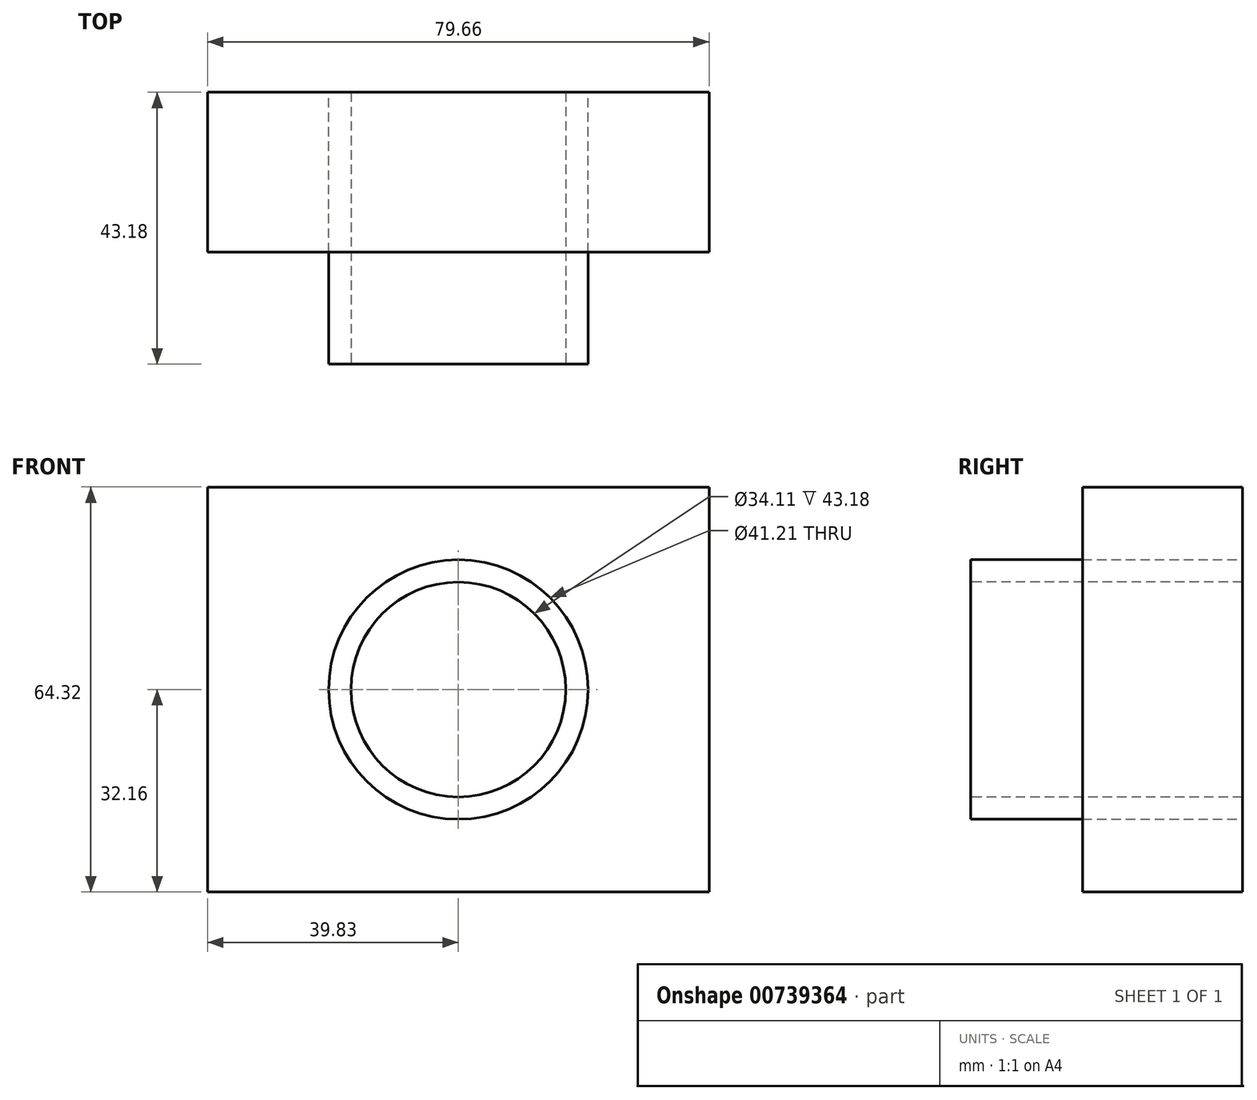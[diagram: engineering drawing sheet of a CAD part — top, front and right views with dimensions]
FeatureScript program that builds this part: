
annotation { "Feature Type Name" : "Feature", "Feature Type Description" : "" }
export const myFeature = defineFeature(function(context is Context, id is Id, definition is map)
    precondition{}
    {
        {
            var Q0;
            Q0=qCreatedBy(makeId("Front.planeOp"),FACE);
            var sketch = newSketch(context, id + "F0", { "sketchPlane" : qUnion([Q0])});
            skLineSegment(sketch, "E0.bottom", {"start": v(39.83, 32.16) * mm, "end": v(-39.83, 32.16) * mm});
            skLineSegment(sketch, "E0.top", {"start": v(39.83, -32.16) * mm, "end": v(-39.83, -32.16) * mm});
            skLineSegment(sketch, "E0.left", {"start": v(39.83, 32.16) * mm, "end": v(39.83, -32.16) * mm});
            skLineSegment(sketch, "E0.right", {"start": v(-39.83, 32.16) * mm, "end": v(-39.83, -32.16) * mm});
            skPoint(sketch, "E0.middle", {"position": v(0, 0) * mm});
            skCircle(sketch, "E1", {"center": v(0, 0) * mm, "radius": 20.6 * mm});
            skSolve(sketch);
        }
        {
            var Q0;
            Q0=makeQuery(id+"F0.imprint","IMPRINT",FACE,{"disambiguationData":[TD([[makeQuery(id+"F0.imprint","IMPRINT",EDGE,{"derivedFrom":sQuery(id+"F0.wireOp",EDGE,"E0.bottom")}),1.0]])]});
            extrude(context, id + "F1", {"entities" : qUnion([Q0]), "depth" : 25.4 * mm, "offsetDistance" : 25.4 * mm});
        }
        {
            var Q0;
            Q0=makeQuery(id+"F1.opExtrude","CAP_FACE",FACE,{"disambiguationData":[OSD([sQuery(id+"F0.wireOp",EDGE,"E0.bottom"),sQuery(id+"F0.wireOp",EDGE,"E0.top"),sQuery(id+"F0.wireOp",EDGE,"E0.left"),sQuery(id+"F0.wireOp",EDGE,"E0.right"),sQuery(id+"F0.wireOp",EDGE,"E1")])],"isStart":true});
            var sketch = newSketch(context, id + "F2", { "sketchPlane" : qUnion([Q0])});
            skLineSegment(sketch, "E2", {"start": v(0, 20.6) * mm, "end": v(0, 17) * mm});
            skLineSegment(sketch, "E3", {"start": v(0, -17) * mm, "end": v(0, -20.6) * mm});
            skLineSegment(sketch, "E4", {"start": v(0, -20.6) * mm, "end": v(0, -17) * mm});
            skSolve(sketch);
        }
        {
            var Q0;
            {var subQ0=makeQuery(id+"F1.opExtrude","CAP_EDGE",EDGE,{"disambiguationData":[OSD([sQuery(id+"F0.wireOp",EDGE,"E1")])],"isStart":true});var subQ1=makeQuery(id+"F2.imprint","IMPRINT",VERTEX,{"disambiguationData":[OD(0.0)],"derivedFrom":subQ0});Q0=makeQuery(id+"F2.imprint","IMPRINT",FACE,{"disambiguationData":[TD([[makeQuery(id+"F2.imprint","IMPRINT",EDGE,{"disambiguationData":[TD([[subQ1,-1.0]])],"derivedFrom":subQ0}),-1.0]])]});}
            extrude(context, id + "F3", {"entities" : qUnion([Q0]), "oppositeDirection" : true, "depth" : 43.18 * mm, "offsetDistance" : 25.4 * mm});
        }
        {
            var Q0;
            Q0=makeQuery(id+"F3.opExtrude","CAP_FACE",FACE,{"disambiguationData":[OSD([sQuery(id+"F0.wireOp",EDGE,"E1")])],"isStart":false});
            var sketch = newSketch(context, id + "F4", { "sketchPlane" : qUnion([Q0])});
            skCircle(sketch, "E5", {"center": v(0, 0) * mm, "radius": 17.06 * mm});
            skSolve(sketch);
        }
        {
            var Q0;
            Q0=makeQuery(id+"F4.imprint","IMPRINT",FACE,{"disambiguationData":[TD([[makeQuery(id+"F4.imprint","IMPRINT",EDGE,{"derivedFrom":sQuery(id+"F4.wireOp",EDGE,"E5")}),1.0]])]});
            extrude(context, id + "F5", {"entities" : qUnion([Q0]), "operationType" : NewBodyOperationType.REMOVE, "oppositeDirection" : true, "depth" : 50.8 * mm, "offsetDistance" : 25.4 * mm});
        }
    });
